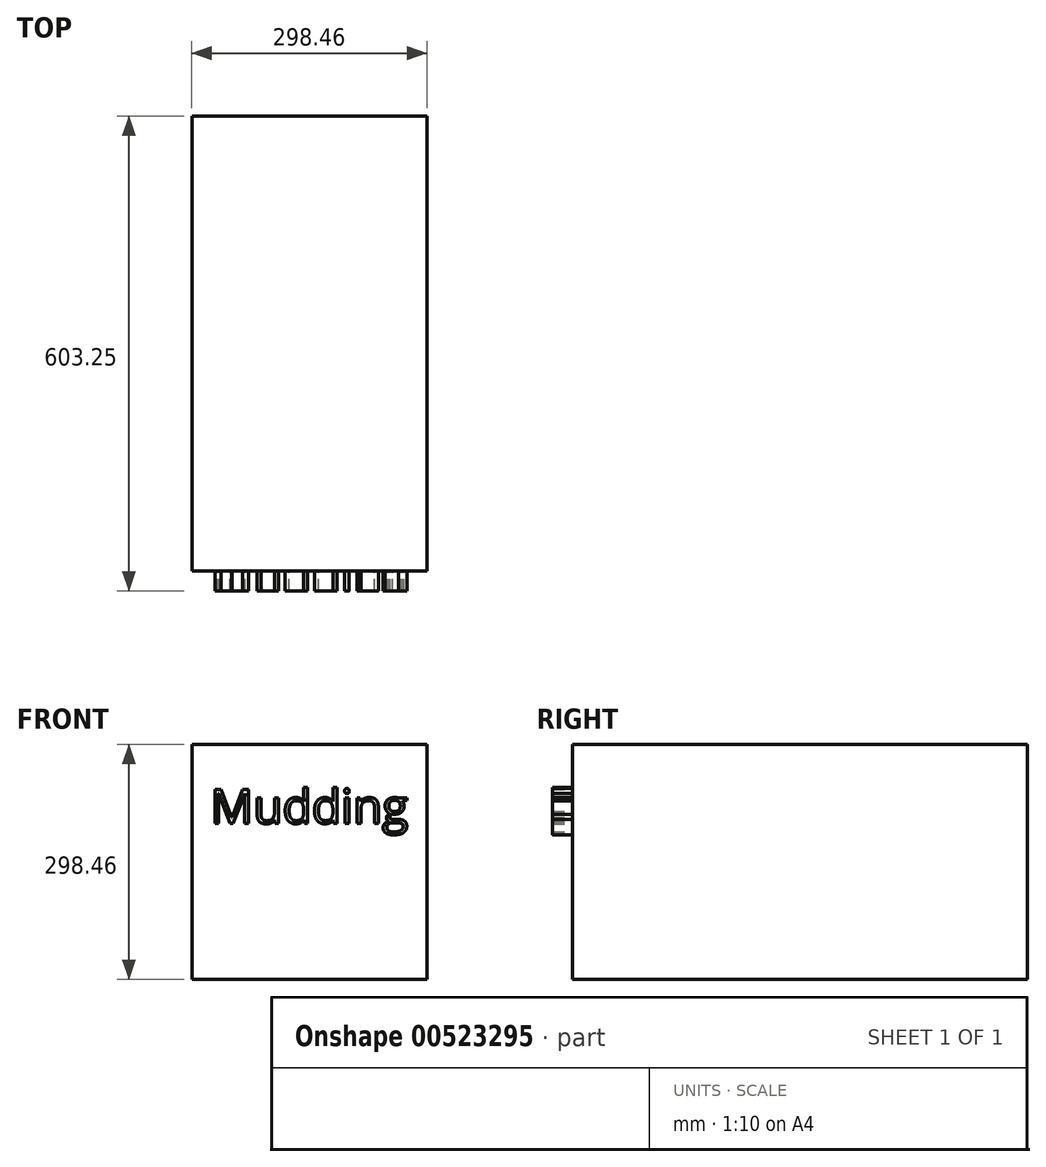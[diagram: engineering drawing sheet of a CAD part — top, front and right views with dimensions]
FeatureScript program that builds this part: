
annotation { "Feature Type Name" : "Feature", "Feature Type Description" : "" }
export const myFeature = defineFeature(function(context is Context, id is Id, definition is map)
    precondition{}
    {
        {
            var Q0;
            Q0=qCreatedBy(makeId("Front.planeOp"),FACE);
            var sketch = newSketch(context, id + "F0", { "sketchPlane" : qUnion([Q0])});
            skLineSegment(sketch, "E0.bottom", {"start": v(149.22, 149.23) * mm, "end": v(-149.23, 149.23) * mm});
            skLineSegment(sketch, "E0.top", {"start": v(149.23, -149.22) * mm, "end": v(-149.22, -149.22) * mm});
            skLineSegment(sketch, "E0.left", {"start": v(149.22, 149.23) * mm, "end": v(149.23, -149.22) * mm});
            skLineSegment(sketch, "E0.right", {"start": v(-149.23, 149.23) * mm, "end": v(-149.22, -149.22) * mm});
            skPoint(sketch, "E0.middle", {"position": v(0, 0) * mm});
            skSolve(sketch);
        }
        {
            var Q0;
            Q0=makeQuery(id+"F0.imprint","IMPRINT",FACE,{"disambiguationData":[TD([[makeQuery(id+"F0.imprint","IMPRINT",EDGE,{"derivedFrom":sQuery(id+"F0.wireOp",EDGE,"E0.bottom")}),1.0]])]});
            extrude(context, id + "F1", {"entities" : qUnion([Q0]), "depth" : 577.85 * mm, "offsetDistance" : 25.4 * mm});
        }
        {
            var Q0;
            Q0=makeQuery(id+"F1.opExtrude","CAP_FACE",FACE,{"disambiguationData":[OSD([sQuery(id+"F0.wireOp",EDGE,"E0.bottom"),sQuery(id+"F0.wireOp",EDGE,"E0.top"),sQuery(id+"F0.wireOp",EDGE,"E0.left"),sQuery(id+"F0.wireOp",EDGE,"E0.right")])],"isStart":false});
            var sketch = newSketch(context, id + "F2", { "sketchPlane" : qUnion([Q0])});
            skText(sketch, "E1", { "text": "Mudding", "fontName": "OpenSans-Regular.ttf"});
            const initialGuessF2  = {"E1": [-0.12579, 0.04891, 1, 0, 0.04357]};
            skSetInitialGuess(sketch, initialGuessF2);
            skSolve(sketch);
        }
        {
            var Q0;
            Q0 = qSketchRegion(id + "F2", true);
            extrude(context, id + "F3", {"entities" : qUnion([Q0]), "operationType" : NewBodyOperationType.ADD, "depth" : 25.4 * mm, "offsetDistance" : 25.4 * mm});
        }
    });
